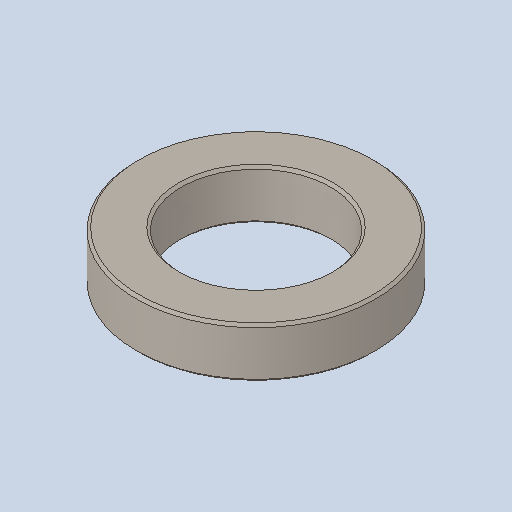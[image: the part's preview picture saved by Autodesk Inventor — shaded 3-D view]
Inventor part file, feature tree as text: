
AUTODESK INVENTOR PART (.ipt)
format: ipt  version: 2023 (Build 270158000, 158)  size: 100,864 bytes
history: native  units: in
note: dims shown in document units (in); Inventor stores cm internally (conversion verified against a paired STEP export)
features: chamfer x1
ambient origin geometry x8: Origin, YZ Plane, XZ Plane, XY Plane, X Axis, Y Axis, Z Axis, Center Point
bodies: Solid1 (feature_tree)
feature tree (1):
  chamfer  "Chamfer1"  [1 undecoded]
note: 1 required parameter value undecoded (feature->parameter linkage not recoverable at this tier; creation-order binding heuristic only, values carry confidence <= 0.55)
